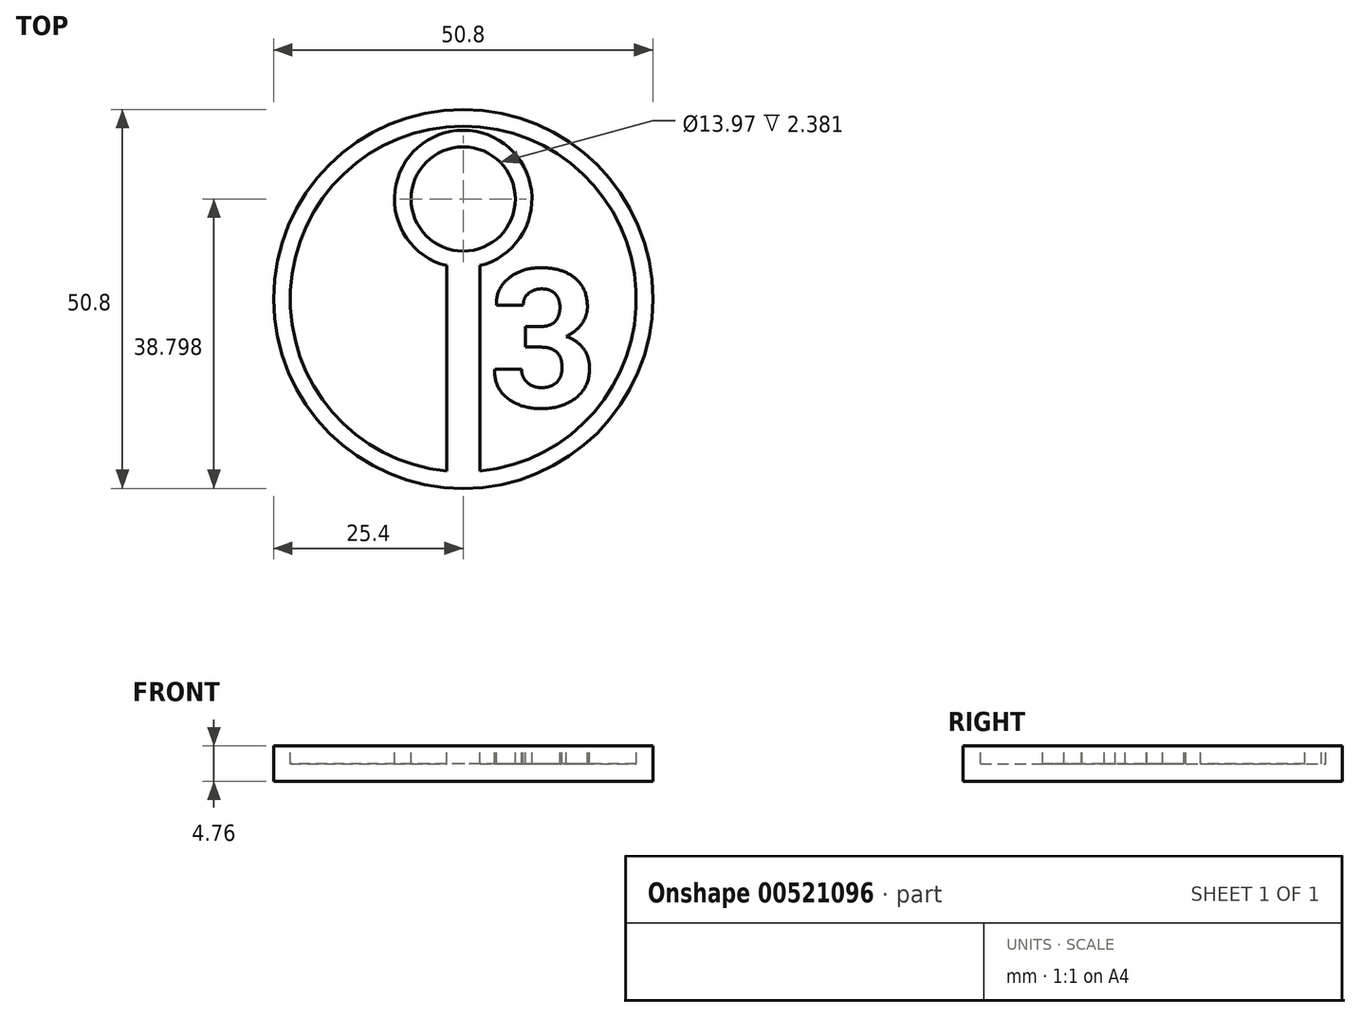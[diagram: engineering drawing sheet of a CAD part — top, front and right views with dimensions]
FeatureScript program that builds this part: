
annotation { "Feature Type Name" : "Feature", "Feature Type Description" : "" }
export const myFeature = defineFeature(function(context is Context, id is Id, definition is map)
    precondition{}
    {
        {
            var Q0;
            Q0=qCreatedBy(makeId("Top.planeOp"),FACE);
            var sketch = newSketch(context, id + "F0", { "sketchPlane" : qUnion([Q0])});
            skCircle(sketch, "E0", {"center": v(0, 0) * mm, "radius": 25.4 * mm});
            skSolve(sketch);
        }
        {
            var Q0;
            Q0=qSketchRegion(id+"F0",true);
            extrude(context, id + "F1", {"entities" : qUnion([Q0]), "depth" : 4.76 * mm, "offsetDistance" : 25.4 * mm});
        }
        {
            var Q0;
            Q0=makeQuery(id+"F1.opExtrude","CAP_FACE",FACE,{"disambiguationData":[OSD([sQuery(id+"F0.wireOp",EDGE,"E0")])],"isStart":false});
            var sketch = newSketch(context, id + "F2", { "sketchPlane" : qUnion([Q0])});
            skCircle(sketch, "E1", {"center": v(0, 0) * mm, "radius": 23.18 * mm});
            skCircle(sketch, "E2", {"center": v(0, 13.4) * mm, "radius": 6.99 * mm});
            skLineSegment(sketch, "E3.0", {"start": v(2.22, -23.07) * mm, "end": v(2.22, 4.46) * mm});
            skLineSegment(sketch, "E4", {"start": v(-2.22, 4.46) * mm, "end": v(-2.22, -23.07) * mm});
            skArc(sketch, "E5", {"start": v(2.22, 4.46) * mm, "mid": v(0, 22.6) * mm, "end": v(-2.22, 4.46) * mm});
            skSolve(sketch);
        }
        {
            var Q0;
            {var subQ0=sQuery(id+"F2.wireOp",EDGE,"E3.0");Q0=makeQuery(id+"F2.imprint","IMPRINT",FACE,{"disambiguationData":[TD([[makeQuery(id+"F2.imprint","IMPRINT",EDGE,{"derivedFrom":subQ0}),-1.0]])]});}
            extrude(context, id + "F3", {"entities" : qUnion([Q0]), "operationType" : NewBodyOperationType.REMOVE, "oppositeDirection" : true, "depth" : 2.38 * mm, "offsetDistance" : 25.4 * mm});
        }
        {
            var Q0;
            Q0=makeQuery(id+"F2.imprint","IMPRINT",FACE,{"disambiguationData":[TD([[makeQuery(id+"F2.imprint","IMPRINT",EDGE,{"derivedFrom":sQuery(id+"F2.wireOp",EDGE,"E2")}),1.0]])]});
            extrude(context, id + "F4", {"entities" : qUnion([Q0]), "operationType" : NewBodyOperationType.REMOVE, "oppositeDirection" : true, "depth" : 2.38 * mm, "offsetDistance" : 25.4 * mm});
        }
        {
            var Q0;
            {var subQ0=sQuery(id+"F2.wireOp",EDGE,"E3.0");Q0=makeQuery(id+"F2.imprint","IMPRINT",FACE,{"disambiguationData":[TD([[makeQuery(id+"F2.imprint","IMPRINT",EDGE,{"derivedFrom":subQ0}),-1.0]])]});}
            var sketch = newSketch(context, id + "F5", { "sketchPlane" : qUnion([Q0])});
            skLineSegment(sketch, "E6.bottom", {"start": v(3.5, 4.16) * mm, "end": v(18.5, 4.16) * mm});
            skLineSegment(sketch, "E6.right", {"start": v(18.5, 4.16) * mm, "end": v(18.5, -14.44) * mm});
            skText(sketch, "E7", { "text": "3", "fontName": "RobotoSlab-Bold.ttf"});
            const initialGuessF5  = {"E7": [0.0035, -0.01444, 1, 0, 0.0186]};
            skSetInitialGuess(sketch, initialGuessF5);
            skSolve(sketch);
        }
        {
            var Q0;
            Q0=qSketchRegion(id+"F5",true);
            extrude(context, id + "F6", {"entities" : qUnion([Q0]), "operationType" : NewBodyOperationType.ADD, "oppositeDirection" : true, "depth" : 2.38 * mm, "offsetDistance" : 25.4 * mm});
        }
    });
